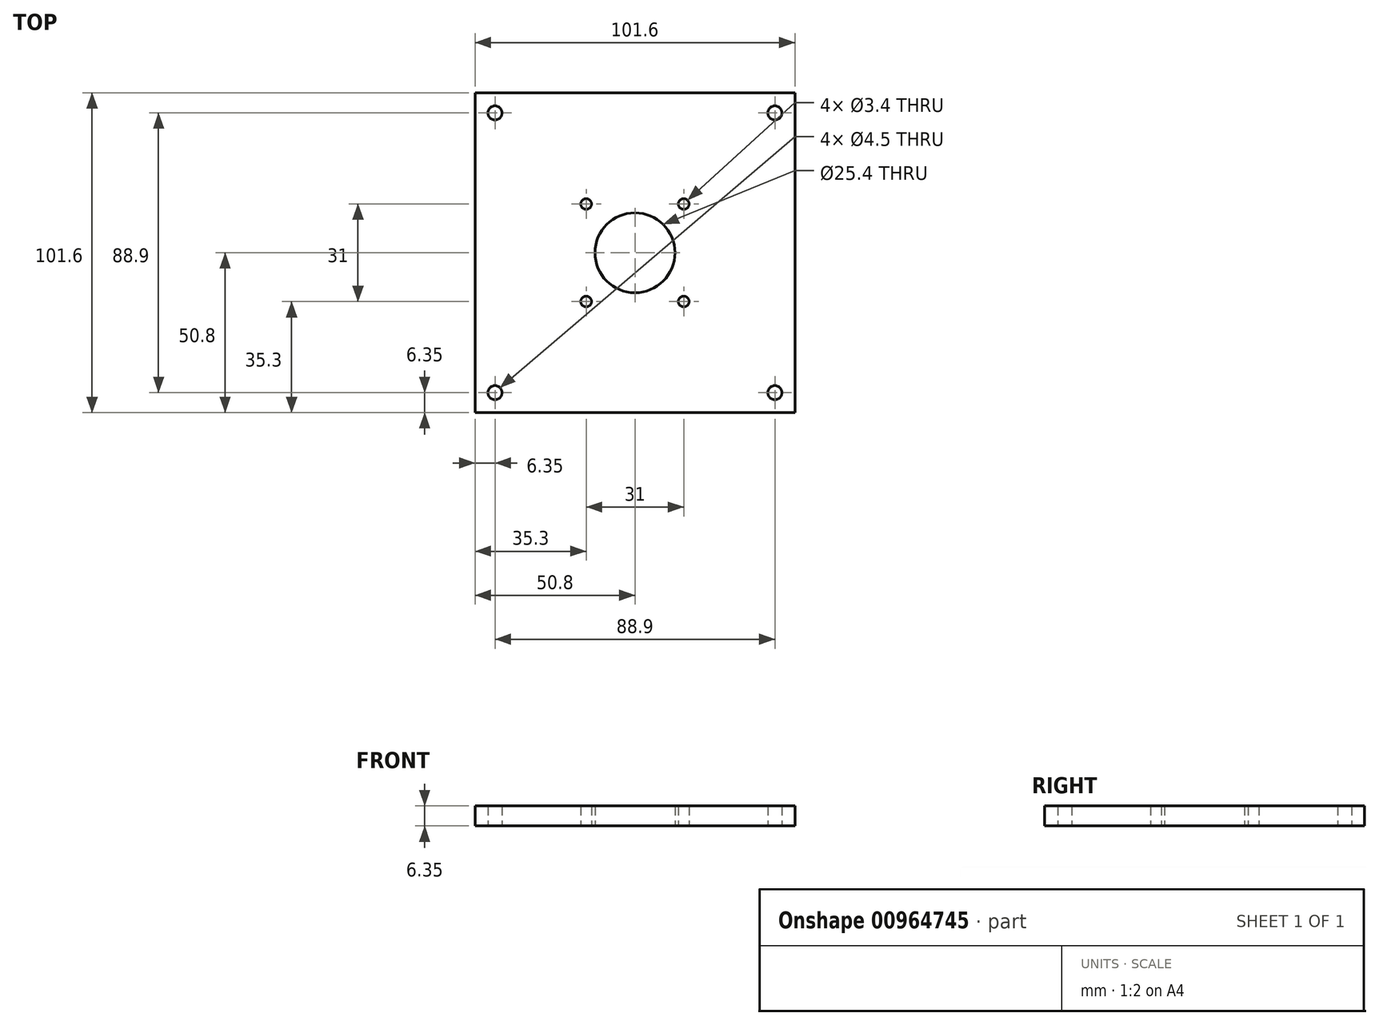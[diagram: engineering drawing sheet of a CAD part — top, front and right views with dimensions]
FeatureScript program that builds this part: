
annotation { "Feature Type Name" : "Feature", "Feature Type Description" : "" }
export const myFeature = defineFeature(function(context is Context, id is Id, definition is map)
    precondition{}
    {
        {
            var Q0;
            Q0=qCreatedBy(makeId("Top.planeOp"),FACE);
            var sketch = newSketch(context, id + "F0", { "sketchPlane" : qUnion([Q0])});
            skLineSegment(sketch, "E0.bottom", {"start": v(50.8, 50.8) * mm, "end": v(-50.8, 50.8) * mm});
            skLineSegment(sketch, "E0.top", {"start": v(50.8, -50.8) * mm, "end": v(-50.8, -50.8) * mm});
            skLineSegment(sketch, "E0.left", {"start": v(50.8, 50.8) * mm, "end": v(50.8, -50.8) * mm});
            skLineSegment(sketch, "E0.right", {"start": v(-50.8, 50.8) * mm, "end": v(-50.8, -50.8) * mm});
            skPoint(sketch, "E0.middle", {"position": v(0, 0) * mm});
            skCircle(sketch, "E1", {"center": v(0, 0) * mm, "radius": 12.7 * mm});
            skCircle(sketch, "E2", {"center": v(-44.45, 44.45) * mm, "radius": 2.25 * mm});
            skCircle(sketch, "E3", {"center": v(44.45, 44.45) * mm, "radius": 2.25 * mm});
            skCircle(sketch, "E4", {"center": v(44.45, -44.45) * mm, "radius": 2.25 * mm});
            skCircle(sketch, "E5", {"center": v(-44.45, -44.45) * mm, "radius": 2.25 * mm});
            skLineSegment(sketch, "E6.bottom", {"start": v(15.5, 15.5) * mm, "end": v(-15.5, 15.5) * mm, "construction": true});
            skLineSegment(sketch, "E6.top", {"start": v(15.5, -15.5) * mm, "end": v(-15.5, -15.5) * mm, "construction": true});
            skLineSegment(sketch, "E6.left", {"start": v(15.5, 15.5) * mm, "end": v(15.5, -15.5) * mm, "construction": true});
            skLineSegment(sketch, "E6.right", {"start": v(-15.5, 15.5) * mm, "end": v(-15.5, -15.5) * mm, "construction": true});
            skCircle(sketch, "E7", {"center": v(-15.5, 15.5) * mm, "radius": 1.7 * mm});
            skCircle(sketch, "E8", {"center": v(15.5, 15.5) * mm, "radius": 1.7 * mm});
            skCircle(sketch, "E9", {"center": v(15.5, -15.5) * mm, "radius": 1.7 * mm});
            skCircle(sketch, "E10", {"center": v(-15.5, -15.5) * mm, "radius": 1.7 * mm});
            skCircle(sketch, "E11", {"center": v(0, 0) * mm, "radius": 21.92 * mm, "construction": true});
            skLineSegment(sketch, "E12.bottom", {"start": v(44.45, 44.45) * mm, "end": v(-44.45, 44.45) * mm, "construction": true});
            skLineSegment(sketch, "E12.top", {"start": v(44.45, -44.45) * mm, "end": v(-44.45, -44.45) * mm, "construction": true});
            skLineSegment(sketch, "E12.left", {"start": v(44.45, 44.45) * mm, "end": v(44.45, -44.45) * mm, "construction": true});
            skLineSegment(sketch, "E12.right", {"start": v(-44.45, 44.45) * mm, "end": v(-44.45, -44.45) * mm, "construction": true});
            skSolve(sketch);
        }
        {
            var Q0;
            Q0 = qSketchRegion(id + "F0", true);
            extrude(context, id + "F1", {"entities" : qUnion([Q0]), "depth" : 6.35 * mm, "offsetDistance" : 25.4 * mm});
        }
    });
